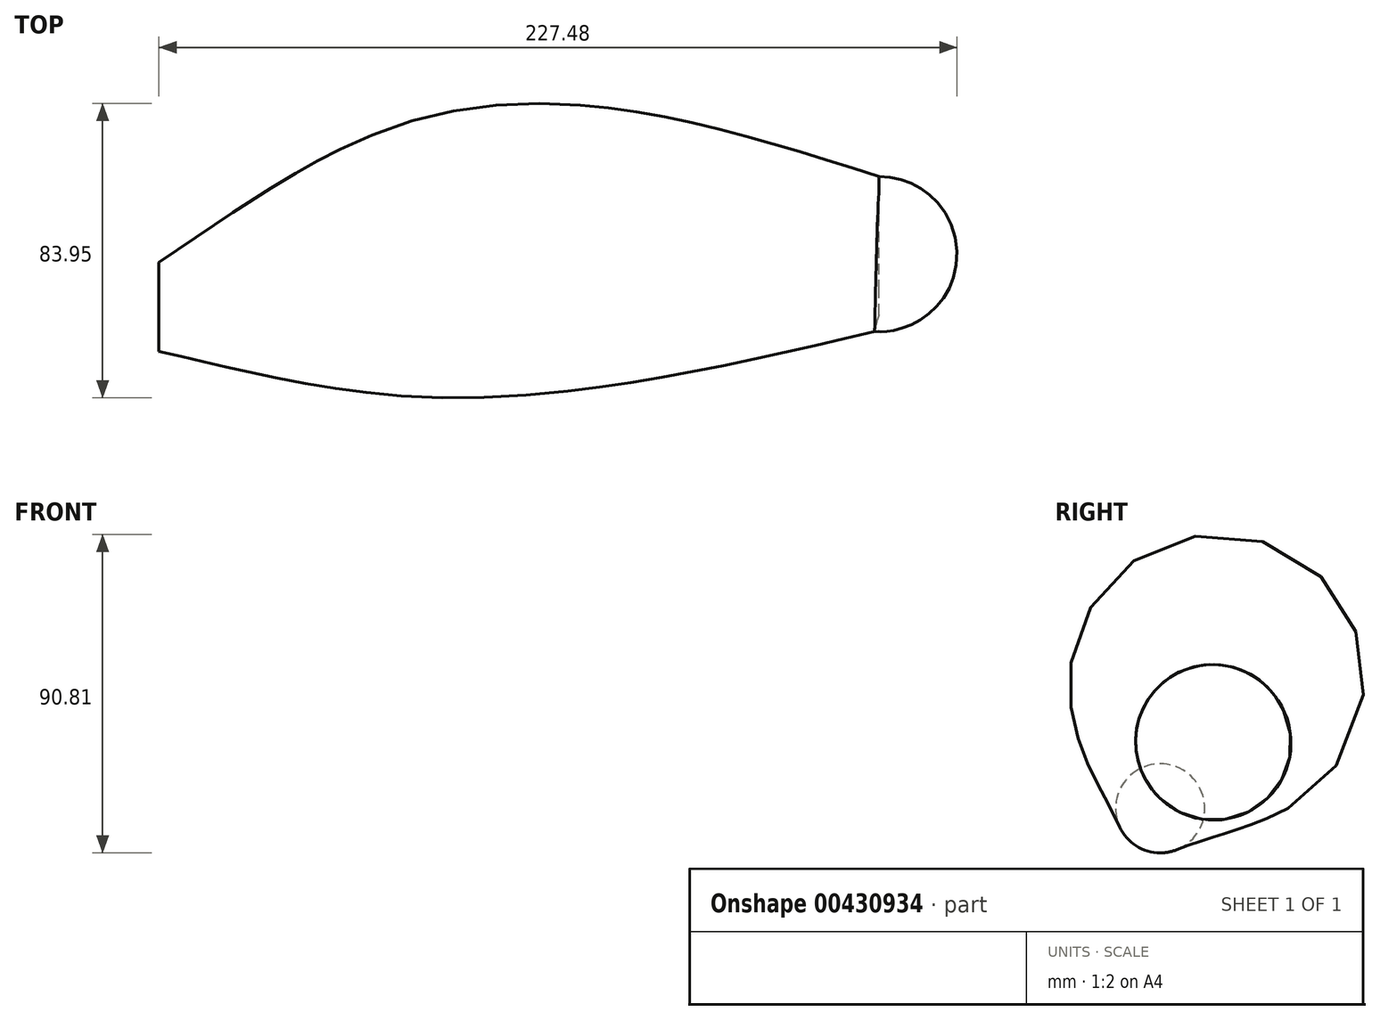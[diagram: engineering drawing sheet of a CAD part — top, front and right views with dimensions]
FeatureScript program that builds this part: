
annotation { "Feature Type Name" : "Feature", "Feature Type Description" : "" }
export const myFeature = defineFeature(function(context is Context, id is Id, definition is map)
    precondition{}
    {
        {
            var Q0;
            Q0=qCreatedBy(makeId("Right.planeOp"),FACE);
            var sketch = newSketch(context, id + "F0", { "sketchPlane" : qUnion([Q0])});
            skCircle(sketch, "E0", {"center": v(-45.45, 17.38) * mm, "radius": 12.7 * mm});
            skSolve(sketch);
        }
        {
            var Q0;
            Q0=qCreatedBy(makeId("Right.planeOp"),FACE);
            cPlane(context, id + "F1", {"entities" : qUnion([Q0]), "cplaneType" : CPlaneType.OFFSET, "offset" : 66.04 * mm, "width" : 152.4 * mm, "height" : 152.4 * mm});
        }
        {
            var Q0;
            Q0=qCreatedBy(id+"F1.planeOp",FACE);
            var sketch = newSketch(context, id + "F2", { "sketchPlane" : qUnion([Q0])});
            skCircle(sketch, "E1", {"center": v(-32.46, 48.55) * mm, "radius": 38.1 * mm});
            skSolve(sketch);
        }
        {
            var Q0;
            Q0=qCreatedBy(id+"F1.planeOp",FACE);
            cPlane(context, id + "F3", {"entities" : qUnion([Q0]), "cplaneType" : CPlaneType.OFFSET, "offset" : 139.2 * mm, "width" : 152.4 * mm, "height" : 152.4 * mm});
        }
        {
            var Q0;
            Q0=qCreatedBy(id+"F3.planeOp",FACE);
            var sketch = newSketch(context, id + "F4", { "sketchPlane" : qUnion([Q0])});
            skCircle(sketch, "E2", {"center": v(-30.18, 36.02) * mm, "radius": 22 * mm});
            skSolve(sketch);
        }
        {
            var Q0;
            Q0=makeQuery(id+"F0.imprint","IMPRINT",FACE,{"disambiguationData":[TD([[makeQuery(id+"F0.imprint","IMPRINT",EDGE,{"derivedFrom":sQuery(id+"F0.wireOp",EDGE,"E0")}),1.0]])]});
            var Q1;
            Q1=makeQuery(id+"F2.imprint","IMPRINT",FACE,{"disambiguationData":[TD([[makeQuery(id+"F2.imprint","IMPRINT",EDGE,{"derivedFrom":sQuery(id+"F2.wireOp",EDGE,"E1")}),1.0]])]});
            var Q2;
            Q2=makeQuery(id+"F4.imprint","IMPRINT",FACE,{"disambiguationData":[TD([[makeQuery(id+"F4.imprint","IMPRINT",EDGE,{"derivedFrom":sQuery(id+"F4.wireOp",EDGE,"E2")}),1.0]])]});
            loft(context, id + "F5", {"sheetProfilesArray" : [{ "sheetProfileEntities" : qUnion([Q0]) }, { "sheetProfileEntities" : qUnion([Q1]) }, { "sheetProfileEntities" : qUnion([Q2]) }]});
        }
        {
            var Q0;
            Q0=makeQuery(id+"F5.opLoft","CAP_FACE",FACE,{"disambiguationData":[OSD([makeQuery(id+"F4.imprint","IMPRINT",FACE,{"disambiguationData":[TD([[makeQuery(id+"F4.imprint","IMPRINT",EDGE,{"derivedFrom":sQuery(id+"F4.wireOp",EDGE,"E2")}),1.0]])]})])],"isStart":true});
            var sketch = newSketch(context, id + "F6", { "sketchPlane" : qUnion([Q0])});
            skLineSegment(sketch, "E3", {"start": v(-12.93, 49.67) * mm, "end": v(-47.74, 22.78) * mm});
            skSolve(sketch);
        }
        {
            var Q0;
            {var subQ0=sQuery(id+"F6.wireOp",EDGE,"E3");Q0=makeQuery(id+"F6.imprint","IMPRINT",FACE,{"disambiguationData":[TD([[makeQuery(id+"F6.imprint","IMPRINT",EDGE,{"derivedFrom":subQ0}),1.0]])]});}
            var Q1;
            Q1=sQuery(id+"F6.wireOp",EDGE,"E3");
            revolve(context, id + "F7", {"operationType" : NewBodyOperationType.ADD, "entities" : qUnion([Q0]), "axis" : qUnion([Q1]), "revolveType" : RevolveType.FULL});
        }
    });
